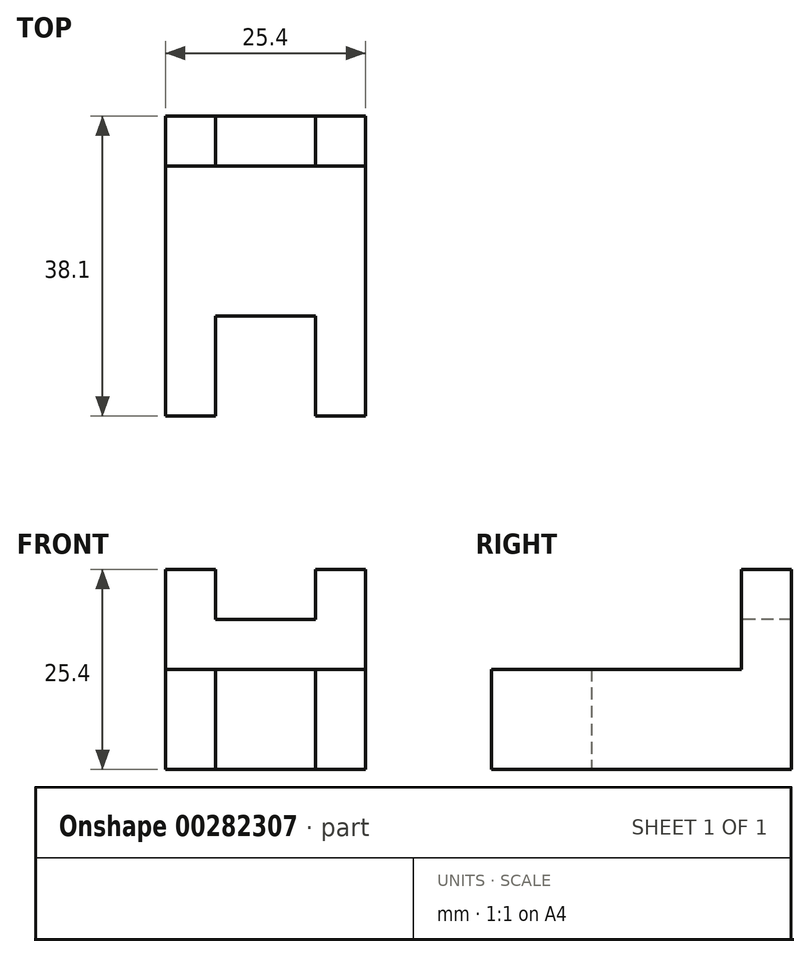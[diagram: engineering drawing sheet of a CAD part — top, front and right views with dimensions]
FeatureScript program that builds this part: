
annotation { "Feature Type Name" : "Feature", "Feature Type Description" : "" }
export const myFeature = defineFeature(function(context is Context, id is Id, definition is map)
    precondition{}
    {
        {
            var Q0;
            Q0=qCreatedBy(makeId("Front.planeOp"),FACE);
            var sketch = newSketch(context, id + "F0", { "sketchPlane" : qUnion([Q0])});
            skLineSegment(sketch, "E0", {"start": v(0, 0) * mm, "end": v(25.4, 0) * mm});
            skLineSegment(sketch, "E1", {"start": v(25.4, 0) * mm, "end": v(25.4, 12.7) * mm});
            skLineSegment(sketch, "E2", {"start": v(25.4, 12.7) * mm, "end": v(0, 12.7) * mm});
            skLineSegment(sketch, "E3", {"start": v(0, 12.7) * mm, "end": v(0, 0) * mm});
            skSolve(sketch);
        }
        {
            var Q0;
            Q0 = qSketchRegion(id + "F0", true);
            extrude(context, id + "F1", {"entities" : qUnion([Q0]), "depth" : 25.4 * mm});
        }
        {
            var Q0;
            Q0=makeQuery(id+"F1.opExtrude","CAP_FACE",FACE,{"disambiguationData":[OSD([sQuery(id+"F0.wireOp",EDGE,"E0"),sQuery(id+"F0.wireOp",EDGE,"E1"),sQuery(id+"F0.wireOp",EDGE,"E2"),sQuery(id+"F0.wireOp",EDGE,"E3")])],"isStart":false});
            var sketch = newSketch(context, id + "F2", { "sketchPlane" : qUnion([Q0])});
            skLineSegment(sketch, "E4", {"start": v(0, 12.7) * mm, "end": v(6.35, 12.7) * mm});
            skLineSegment(sketch, "E5", {"start": v(6.35, 12.7) * mm, "end": v(6.35, 0) * mm});
            skLineSegment(sketch, "E6", {"start": v(6.35, 0) * mm, "end": v(0, 0) * mm});
            skLineSegment(sketch, "E7", {"start": v(0, 0) * mm, "end": v(0, 12.7) * mm});
            skLineSegment(sketch, "E8", {"start": v(25.4, 12.7) * mm, "end": v(19.05, 12.7) * mm});
            skLineSegment(sketch, "E9", {"start": v(19.05, 12.7) * mm, "end": v(19.05, 0) * mm});
            skLineSegment(sketch, "E10", {"start": v(19.05, 0) * mm, "end": v(25.4, 0) * mm});
            skLineSegment(sketch, "E11", {"start": v(25.4, 0) * mm, "end": v(25.4, 12.7) * mm});
            skSolve(sketch);
        }
        {
            var Q0;
            Q0 = qSketchRegion(id + "F2", true);
            extrude(context, id + "F3", {"entities" : qUnion([Q0]), "operationType" : NewBodyOperationType.ADD, "depth" : 12.7 * mm});
        }
        {
            var Q0;
            Q0=makeQuery(id+"F3.boolean.opBoolean","MERGE",FACE,{"derivedFrom":[makeQuery(id+"F1.opExtrude","SWEPT_FACE",FACE,{"disambiguationData":[OSD([sQuery(id+"F0.wireOp",EDGE,"E2")])]}),makeQuery(id+"F3.opExtrude","SWEPT_FACE",FACE,{"disambiguationData":[OSD([sQuery(id+"F2.wireOp",EDGE,"E4")])]}),makeQuery(id+"F3.opExtrude","SWEPT_FACE",FACE,{"disambiguationData":[OSD([sQuery(id+"F2.wireOp",EDGE,"E8")])]})]});
            var sketch = newSketch(context, id + "F4", { "sketchPlane" : qUnion([Q0])});
            skLineSegment(sketch, "E12", {"start": v(0, 0) * mm, "end": v(0, -6.35) * mm});
            skLineSegment(sketch, "E13", {"start": v(0, -6.35) * mm, "end": v(25.4, -6.35) * mm});
            skLineSegment(sketch, "E14", {"start": v(25.4, -6.35) * mm, "end": v(25.4, 0) * mm});
            skLineSegment(sketch, "E15", {"start": v(25.4, 0) * mm, "end": v(0, 0) * mm});
            skSolve(sketch);
        }
        {
            var Q0;
            Q0=makeQuery(id+"F4.imprint","IMPRINT",FACE,{"disambiguationData":[TD([[makeQuery(id+"F4.imprint","IMPRINT",EDGE,{"derivedFrom":sQuery(id+"F4.wireOp",EDGE,"E12")}),-1.0]])]});
            extrude(context, id + "F5", {"entities" : qUnion([Q0]), "operationType" : NewBodyOperationType.ADD, "depth" : 6.35 * mm});
        }
        {
            var Q0;
            Q0=makeQuery(id+"F5.opExtrude","CAP_FACE",FACE,{"disambiguationData":[OSD([sQuery(id+"F4.wireOp",EDGE,"E12"),sQuery(id+"F4.wireOp",EDGE,"E13"),sQuery(id+"F4.wireOp",EDGE,"E14"),sQuery(id+"F4.wireOp",EDGE,"E15")])],"isStart":false});
            var sketch = newSketch(context, id + "F6", { "sketchPlane" : qUnion([Q0])});
            skLineSegment(sketch, "E16", {"start": v(0, 0) * mm, "end": v(6.35, 0) * mm});
            skLineSegment(sketch, "E17", {"start": v(6.35, 0) * mm, "end": v(6.35, -6.35) * mm});
            skLineSegment(sketch, "E18", {"start": v(6.35, -6.35) * mm, "end": v(0, -6.35) * mm});
            skLineSegment(sketch, "E19", {"start": v(0, -6.35) * mm, "end": v(0, 0) * mm});
            skLineSegment(sketch, "E20", {"start": v(25.4, 0) * mm, "end": v(19.05, 0) * mm});
            skLineSegment(sketch, "E21", {"start": v(19.05, 0) * mm, "end": v(19.05, -6.35) * mm});
            skLineSegment(sketch, "E22", {"start": v(19.05, -6.35) * mm, "end": v(25.4, -6.35) * mm});
            skLineSegment(sketch, "E23", {"start": v(25.4, -6.35) * mm, "end": v(25.4, 0) * mm});
            skSolve(sketch);
        }
        {
            var Q0;
            Q0 = qSketchRegion(id + "F6", true);
            extrude(context, id + "F7", {"entities" : qUnion([Q0]), "operationType" : NewBodyOperationType.ADD, "depth" : 6.35 * mm});
        }
    });
